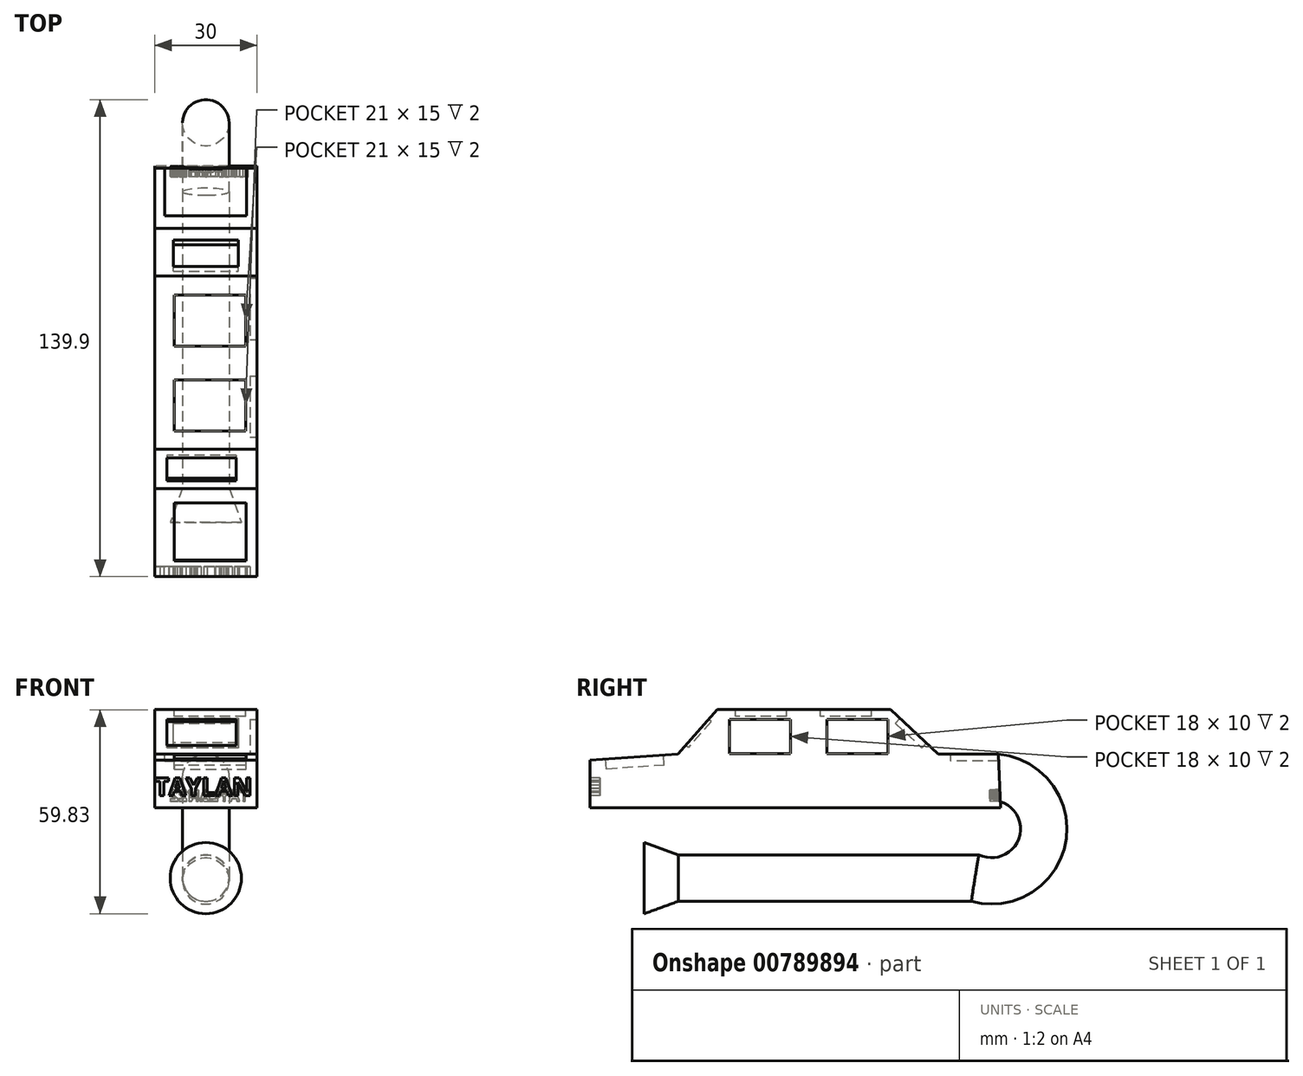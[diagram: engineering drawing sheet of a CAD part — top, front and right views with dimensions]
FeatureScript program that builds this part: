
annotation { "Feature Type Name" : "Feature", "Feature Type Description" : "" }
export const myFeature = defineFeature(function(context is Context, id is Id, definition is map)
    precondition{}
    {
        {
            var Q0;
            Q0=qCreatedBy(makeId("Right.planeOp"),FACE);
            var sketch = newSketch(context, id + "F0", { "sketchPlane" : qUnion([Q0])});
            skLineSegment(sketch, "E0", {"start": v(-63.91, 0) * mm, "end": v(56.54, 0) * mm});
            skLineSegment(sketch, "E1", {"start": v(-63.91, 0) * mm, "end": v(-63.91, 14.06) * mm});
            skLineSegment(sketch, "E2", {"start": v(-63.91, 14.06) * mm, "end": v(-38.11, 15.8) * mm});
            skLineSegment(sketch, "E3", {"start": v(-38.11, 15.8) * mm, "end": v(-26.48, 28.8) * mm});
            skLineSegment(sketch, "E4", {"start": v(-26.48, 28.8) * mm, "end": v(1.84, 28.8) * mm});
            skLineSegment(sketch, "E5", {"start": v(1.84, 28.8) * mm, "end": v(24.34, 28.8) * mm});
            skLineSegment(sketch, "E6", {"start": v(24.34, 28.8) * mm, "end": v(38.3, 15.8) * mm});
            skLineSegment(sketch, "E7", {"start": v(38.3, 15.8) * mm, "end": v(55.96, 15.8) * mm});
            skLineSegment(sketch, "E8", {"start": v(55.96, 15.8) * mm, "end": v(56.54, 0) * mm});
            skSolve(sketch);
        }
        {
            var Q0;
            Q0=makeQuery(id+"F0.imprint","IMPRINT",FACE,{"disambiguationData":[TD([[makeQuery(id+"F0.imprint","IMPRINT",EDGE,{"derivedFrom":sQuery(id+"F0.wireOp",EDGE,"E0")}),1.0]])]});
            extrude(context, id + "F1", {"entities" : qUnion([Q0]), "depth" : 15 * mm, "offsetDistance" : 25 * mm});
        }
        {
            var Q0;
            Q0=makeQuery(id+"F1.opExtrude","SWEPT_BODY",BODY,{"disambiguationData":[OSD([sQuery(id+"F0.wireOp",EDGE,"E0"),sQuery(id+"F0.wireOp",EDGE,"E1"),sQuery(id+"F0.wireOp",EDGE,"E2"),sQuery(id+"F0.wireOp",EDGE,"E3"),sQuery(id+"F0.wireOp",EDGE,"E4"),sQuery(id+"F0.wireOp",EDGE,"E5"),sQuery(id+"F0.wireOp",EDGE,"E6"),sQuery(id+"F0.wireOp",EDGE,"E7"),sQuery(id+"F0.wireOp",EDGE,"E8")])]});
            var Q1;
            Q1=qCreatedBy(makeId("Right.planeOp"),FACE);
            mirror(context, id + "F2", {"operationType" : NewBodyOperationType.ADD, "entities" : qUnion([Q0]), "mirrorPlane" : qUnion([Q1])});
        }
        {
            var Q0;
            {var subQ0=makeQuery(id+"F1.opExtrude","SWEPT_FACE",FACE,{"disambiguationData":[OSD([sQuery(id+"F0.wireOp",EDGE,"E3")])]});Q0=makeQuery(id+"F2.boolean.opBoolean","MERGE",FACE,{"derivedFrom":[subQ0,makeQuery(id+"F2.opPattern","COPY",FACE,{"derivedFrom":subQ0,"instanceName":"1"})]});}
            var sketch = newSketch(context, id + "F3", { "sketchPlane" : qUnion([Q0])});
            skLineSegment(sketch, "E9", {"start": v(-11.4, 0) * mm, "end": v(-11.4, -10.22) * mm});
            skLineSegment(sketch, "E10", {"start": v(-11.4, -10.22) * mm, "end": v(8.86, -10.22) * mm});
            skLineSegment(sketch, "E11", {"start": v(8.86, -10.22) * mm, "end": v(8.86, 0) * mm});
            skLineSegment(sketch, "E12", {"start": v(8.86, 0) * mm, "end": v(-11.4, 0) * mm});
            skSolve(sketch);
        }
        {
            var Q0;
            Q0=makeQuery(id+"F3.imprint","IMPRINT",FACE,{"disambiguationData":[TD([[makeQuery(id+"F3.imprint","IMPRINT",EDGE,{"derivedFrom":sQuery(id+"F3.wireOp",EDGE,"E9")}),1.0]])]});
            extrude(context, id + "F4", {"entities" : qUnion([Q0]), "operationType" : NewBodyOperationType.REMOVE, "oppositeDirection" : true, "depth" : 1 * mm, "offsetDistance" : 25 * mm});
        }
        {
            var Q0;
            Q0=makeQuery(id+"F1.opExtrude","CAP_FACE",FACE,{"disambiguationData":[OSD([sQuery(id+"F0.wireOp",EDGE,"E0"),sQuery(id+"F0.wireOp",EDGE,"E1"),sQuery(id+"F0.wireOp",EDGE,"E2"),sQuery(id+"F0.wireOp",EDGE,"E3"),sQuery(id+"F0.wireOp",EDGE,"E4"),sQuery(id+"F0.wireOp",EDGE,"E5"),sQuery(id+"F0.wireOp",EDGE,"E6"),sQuery(id+"F0.wireOp",EDGE,"E7"),sQuery(id+"F0.wireOp",EDGE,"E8")])],"isStart":false});
            var sketch = newSketch(context, id + "F5", { "sketchPlane" : qUnion([Q0])});
            skLineSegment(sketch, "E13", {"start": v(-23, 25.97) * mm, "end": v(-23, 15.97) * mm});
            skLineSegment(sketch, "E14", {"start": v(-23, 15.97) * mm, "end": v(-5, 15.97) * mm});
            skLineSegment(sketch, "E15", {"start": v(-5, 15.97) * mm, "end": v(-5, 25.97) * mm});
            skLineSegment(sketch, "E16", {"start": v(-5, 25.97) * mm, "end": v(-23, 25.97) * mm});
            skLineSegment(sketch, "E17", {"start": v(5.59, 25.97) * mm, "end": v(5.59, 15.97) * mm});
            skPoint(sketch, "E17.startSnap0", {"position": v(-14, 25.97) * mm});
            skLineSegment(sketch, "E18", {"start": v(5.59, 15.97) * mm, "end": v(23.59, 15.97) * mm});
            skLineSegment(sketch, "E19", {"start": v(23.59, 15.97) * mm, "end": v(23.59, 25.97) * mm});
            skLineSegment(sketch, "E20", {"start": v(23.59, 25.97) * mm, "end": v(5.59, 25.97) * mm});
            skSolve(sketch);
        }
        {
            var Q0;
            Q0=makeQuery(id+"F5.imprint","IMPRINT",FACE,{"disambiguationData":[TD([[makeQuery(id+"F5.imprint","IMPRINT",EDGE,{"derivedFrom":sQuery(id+"F5.wireOp",EDGE,"E13")}),1.0]])]});
            var Q1;
            Q1=makeQuery(id+"F5.imprint","IMPRINT",FACE,{"disambiguationData":[TD([[makeQuery(id+"F5.imprint","IMPRINT",EDGE,{"derivedFrom":sQuery(id+"F5.wireOp",EDGE,"E17")}),1.0]])]});
            extrude(context, id + "F6", {"entities" : qUnion([Q0, Q1]), "operationType" : NewBodyOperationType.REMOVE, "oppositeDirection" : true, "depth" : 2 * mm, "offsetDistance" : 25 * mm});
        }
        {
            var Q0;
            {var subQ0=makeQuery(id+"F1.opExtrude","SWEPT_FACE",FACE,{"disambiguationData":[OSD([sQuery(id+"F0.wireOp",EDGE,"E1")])]});Q0=makeQuery(id+"F2.boolean.opBoolean","MERGE",FACE,{"derivedFrom":[subQ0,makeQuery(id+"F2.opPattern","COPY",FACE,{"derivedFrom":subQ0,"instanceName":"1"})]});}
            var sketch = newSketch(context, id + "F7", { "sketchPlane" : qUnion([Q0])});
            skText(sketch, "E21", { "text": "TAYLAN", "fontName": "OpenSans-Bold.ttf"});
            const initialGuessF7  = {"E21": [-0.015, 0.0036, 1, 0, 0.0052]};
            skSetInitialGuess(sketch, initialGuessF7);
            skSolve(sketch);
        }
        {
            var Q0;
            Q0 = qSketchRegion(id + "F7", true);
            extrude(context, id + "F8", {"entities" : qUnion([Q0]), "operationType" : NewBodyOperationType.REMOVE, "oppositeDirection" : true, "depth" : 3 * mm, "offsetDistance" : 25 * mm});
        }
        {
            var Q0;
            {var subQ0=makeQuery(id+"F1.opExtrude","SWEPT_FACE",FACE,{"disambiguationData":[OSD([sQuery(id+"F0.wireOp",EDGE,"E6")])]});Q0=makeQuery(id+"F2.boolean.opBoolean","MERGE",FACE,{"derivedFrom":[subQ0,makeQuery(id+"F2.opPattern","COPY",FACE,{"derivedFrom":subQ0,"instanceName":"1"})]});}
            var sketch = newSketch(context, id + "F9", { "sketchPlane" : qUnion([Q0])});
            skLineSegment(sketch, "E22", {"start": v(9.48, 1.87) * mm, "end": v(9.48, 12.54) * mm});
            skLineSegment(sketch, "E23", {"start": v(9.48, 12.54) * mm, "end": v(-9.51, 12.54) * mm});
            skLineSegment(sketch, "E24", {"start": v(-9.51, 12.54) * mm, "end": v(-9.51, 1.87) * mm});
            skLineSegment(sketch, "E25", {"start": v(-9.51, 1.87) * mm, "end": v(9.48, 1.87) * mm});
            skSolve(sketch);
        }
        {
            var Q0;
            Q0=makeQuery(id+"F9.imprint","IMPRINT",FACE,{"disambiguationData":[TD([[makeQuery(id+"F9.imprint","IMPRINT",EDGE,{"derivedFrom":sQuery(id+"F9.wireOp",EDGE,"E22")}),1.0]])]});
            extrude(context, id + "F10", {"entities" : qUnion([Q0]), "operationType" : NewBodyOperationType.REMOVE, "oppositeDirection" : true, "depth" : 2 * mm, "offsetDistance" : 25 * mm});
        }
        {
            var Q0;
            {var subQ0=makeQuery(id+"F1.opExtrude","SWEPT_FACE",FACE,{"disambiguationData":[OSD([sQuery(id+"F0.wireOp",EDGE,"E8")])]});Q0=makeQuery(id+"F2.boolean.opBoolean","MERGE",FACE,{"derivedFrom":[subQ0,makeQuery(id+"F2.opPattern","COPY",FACE,{"derivedFrom":subQ0,"instanceName":"1"})]});}
            var sketch = newSketch(context, id + "F11", { "sketchPlane" : qUnion([Q0])});
            skText(sketch, "E26", { "text": "TAYLAN22", "fontName": "OpenSans-Bold.ttf"});
            const initialGuessF11  = {"E26": [-0.01253, 0, 1, 0, 0.00326]};
            skSetInitialGuess(sketch, initialGuessF11);
            skSolve(sketch);
        }
        {
            var Q0;
            Q0 = qSketchRegion(id + "F11", true);
            extrude(context, id + "F12", {"entities" : qUnion([Q0]), "operationType" : NewBodyOperationType.REMOVE, "oppositeDirection" : true, "depth" : 3 * mm, "offsetDistance" : 25 * mm});
        }
        {
            var Q0;
            {var subQ0=makeQuery(id+"F1.opExtrude","SWEPT_FACE",FACE,{"disambiguationData":[OSD([sQuery(id+"F0.wireOp",EDGE,"E4"),sQuery(id+"F0.wireOp",EDGE,"E5")])]});Q0=makeQuery(id+"F2.boolean.opBoolean","MERGE",FACE,{"derivedFrom":[subQ0,makeQuery(id+"F2.opPattern","COPY",FACE,{"derivedFrom":subQ0,"instanceName":"1"})]});}
            var sketch = newSketch(context, id + "F13", { "sketchPlane" : qUnion([Q0])});
            skLineSegment(sketch, "E27", {"start": v(-9.32, 18.7) * mm, "end": v(-9.32, 3.7) * mm});
            skLineSegment(sketch, "E28", {"start": v(-9.32, 3.7) * mm, "end": v(11.68, 3.7) * mm});
            skLineSegment(sketch, "E29", {"start": v(11.68, 3.7) * mm, "end": v(11.68, 18.7) * mm});
            skLineSegment(sketch, "E30", {"start": v(11.68, 18.7) * mm, "end": v(-9.32, 18.7) * mm});
            skLineSegment(sketch, "E31", {"start": v(-9.32, -6.16) * mm, "end": v(-9.32, -21.16) * mm});
            skLineSegment(sketch, "E32", {"start": v(-9.32, -21.16) * mm, "end": v(11.68, -21.16) * mm});
            skLineSegment(sketch, "E33", {"start": v(11.68, -21.16) * mm, "end": v(11.68, -6.16) * mm});
            skLineSegment(sketch, "E34", {"start": v(11.68, -6.16) * mm, "end": v(-9.32, -6.16) * mm});
            skSolve(sketch);
        }
        {
            var Q0;
            Q0=makeQuery(id+"F13.imprint","IMPRINT",FACE,{"disambiguationData":[TD([[makeQuery(id+"F13.imprint","IMPRINT",EDGE,{"derivedFrom":sQuery(id+"F13.wireOp",EDGE,"E27")}),1.0]])]});
            var Q1;
            Q1=makeQuery(id+"F13.imprint","IMPRINT",FACE,{"disambiguationData":[TD([[makeQuery(id+"F13.imprint","IMPRINT",EDGE,{"derivedFrom":sQuery(id+"F13.wireOp",EDGE,"E31")}),1.0]])]});
            extrude(context, id + "F14", {"entities" : qUnion([Q0, Q1]), "operationType" : NewBodyOperationType.REMOVE, "oppositeDirection" : true, "depth" : 2 * mm, "offsetDistance" : 25 * mm});
        }
        {
            var Q0;
            {var subQ0=makeQuery(id+"F1.opExtrude","SWEPT_FACE",FACE,{"disambiguationData":[OSD([sQuery(id+"F0.wireOp",EDGE,"E2")])]});Q0=makeQuery(id+"F2.boolean.opBoolean","MERGE",FACE,{"derivedFrom":[subQ0,makeQuery(id+"F2.opPattern","COPY",FACE,{"derivedFrom":subQ0,"instanceName":"1"})]});}
            var sketch = newSketch(context, id + "F15", { "sketchPlane" : qUnion([Q0])});
            skLineSegment(sketch, "E35", {"start": v(-9.2, -41.17) * mm, "end": v(-9.2, -58.17) * mm});
            skLineSegment(sketch, "E36", {"start": v(-9.2, -58.17) * mm, "end": v(11.8, -58.17) * mm});
            skLineSegment(sketch, "E37", {"start": v(11.8, -58.17) * mm, "end": v(11.8, -41.17) * mm});
            skLineSegment(sketch, "E38", {"start": v(11.8, -41.17) * mm, "end": v(-9.2, -41.17) * mm});
            skLineSegment(sketch, "E39", {"start": v(-9.2, 56.29) * mm, "end": v(-9.2, 42.29) * mm});
            skLineSegment(sketch, "E40", {"start": v(-9.2, 42.29) * mm, "end": v(11.8, 42.29) * mm});
            skLineSegment(sketch, "E41", {"start": v(11.8, 42.29) * mm, "end": v(11.8, 56.29) * mm});
            skLineSegment(sketch, "E42", {"start": v(11.8, 56.29) * mm, "end": v(-9.2, 56.29) * mm});
            skSolve(sketch);
        }
        {
            var Q0;
            Q0=makeQuery(id+"F15.imprint","IMPRINT",FACE,{"disambiguationData":[TD([[makeQuery(id+"F15.imprint","IMPRINT",EDGE,{"derivedFrom":sQuery(id+"F15.wireOp",EDGE,"E35")}),1.0]])]});
            var Q1;
            Q1=makeQuery(id+"F15.imprint","IMPRINT",FACE,{"disambiguationData":[TD([[makeQuery(id+"F15.imprint","IMPRINT",EDGE,{"derivedFrom":sQuery(id+"F15.wireOp",EDGE,"E39")}),1.0]])]});
            extrude(context, id + "F16", {"entities" : qUnion([Q0, Q1]), "operationType" : NewBodyOperationType.REMOVE, "oppositeDirection" : true, "depth" : 3 * mm, "offsetDistance" : 25 * mm});
        }
        {
            var Q0;
            {var subQ0=makeQuery(id+"F1.opExtrude","SWEPT_FACE",FACE,{"disambiguationData":[OSD([sQuery(id+"F0.wireOp",EDGE,"E7")])]});Q0=makeQuery(id+"F2.boolean.opBoolean","MERGE",FACE,{"derivedFrom":[subQ0,makeQuery(id+"F2.opPattern","COPY",FACE,{"derivedFrom":subQ0,"instanceName":"1"})]});}
            var sketch = newSketch(context, id + "F17", { "sketchPlane" : qUnion([Q0])});
            skLineSegment(sketch, "E43", {"start": v(0, 55.9) * mm, "end": v(-12, 55.9) * mm});
            skLineSegment(sketch, "E44", {"start": v(-12, 55.9) * mm, "end": v(-12, 41.9) * mm});
            skLineSegment(sketch, "E45", {"start": v(-12, 41.9) * mm, "end": v(0, 41.9) * mm});
            skLineSegment(sketch, "E46.MirrorCS", {"start": v(0, 55.9) * mm, "end": v(12, 55.9) * mm});
            skLineSegment(sketch, "E47.MirrorCS", {"start": v(12, 55.9) * mm, "end": v(12, 41.9) * mm});
            skLineSegment(sketch, "E48.MirrorCS", {"start": v(12, 41.9) * mm, "end": v(0, 41.9) * mm});
            skSolve(sketch);
        }
        {
            var Q0;
            Q0 = qSketchRegion(id + "F17", true);
            extrude(context, id + "F18", {"entities" : qUnion([Q0]), "operationType" : NewBodyOperationType.REMOVE, "oppositeDirection" : true, "depth" : 2 * mm, "offsetDistance" : 25 * mm});
        }
        {
            var Q0;
            Q0=qCreatedBy(makeId("Right.planeOp"),FACE);
            var sketch = newSketch(context, id + "F19", { "sketchPlane" : qUnion([Q0])});
            skArc(sketch, "E49", {"start": v(49.03, -20.59) * mm, "mid": v(68.86, -9.32) * mm, "end": v(55.27, 9) * mm});
            skLineSegment(sketch, "E50", {"start": v(49.03, -20.59) * mm, "end": v(-13.1, -20.59) * mm});
            skLineSegment(sketch, "E51", {"start": v(-37.93, -20.59) * mm, "end": v(-13.1, -20.59) * mm});
            skSolve(sketch);
        }
        {
            var Q0;
            Q0=qCreatedBy(makeId("Front.planeOp"),FACE);
            var sketch = newSketch(context, id + "F20", { "sketchPlane" : qUnion([Q0])});
            skCircle(sketch, "E52", {"center": v(0, -20.59) * mm, "radius": 6.8 * mm});
            skSolve(sketch);
        }
        {
            var Q0;
            Q0=makeQuery(id+"F20.imprint","IMPRINT",FACE,{"disambiguationData":[TD([[makeQuery(id+"F20.imprint","IMPRINT",EDGE,{"derivedFrom":sQuery(id+"F20.wireOp",EDGE,"E52")}),1.0]])]});
            var Q1;
            Q1=sQuery(id+"F19.wireOp",EDGE,"E50");
            var Q2;
            Q2=sQuery(id+"F19.wireOp",EDGE,"E51");
            var Q3;
            Q3=sQuery(id+"F19.wireOp",EDGE,"E49");
            sweep(context, id + "F21", {"operationType" : NewBodyOperationType.ADD, "profiles" : qUnion([Q0]), "path" : qUnion([Q1, Q2, Q3])});
        }
        {
            var Q0;
            Q0=makeQuery(id+"F21.opSweep","CAP_FACE",FACE,{"disambiguationData":[OSD([sQuery(id+"F19.wireOp",VERTEX,"E51.start"),sQuery(id+"F20.wireOp",EDGE,"E52")])],"isStart":false});
            extrude(context, id + "F22", {"entities" : qUnion([Q0]), "operationType" : NewBodyOperationType.ADD, "depth" : 10 * mm, "offsetDistance" : 25 * mm, "hasDraft" : true, "draftAngle" : 20 * degree});
        }
    });
